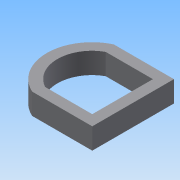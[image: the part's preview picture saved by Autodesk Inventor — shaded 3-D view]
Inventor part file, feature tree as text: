
AUTODESK INVENTOR PART (.ipt)
format: ipt  version: 2015 (Build 190159000, 159)  size: 97,280 bytes
history: native  units: in
note: dims shown in document units (in); Inventor stores cm internally (conversion verified against a paired STEP export)
features: extrude x1, sketch x1
ambient origin geometry x8: Origin, YZ Plane, XZ Plane, XY Plane, X Axis, Y Axis, Z Axis, Center Point
bodies: Body1 (feature_tree)
feature tree (2):
  extrude  "Extrusion2"  Depth=0.25in
  sketch  "Sketch1"  dims[d0=0.41in d1=0.56in d2=0.72in d3=0.573in d4=0.55in d5=0.71in d6=0.6in d7=0.55in d8=0.71in d10=0.55in d11=0.71in d13=0.125in d14=0.125in d15=0.125in d19=0.41in d20=0.125in d21=0.25in d22=0.0in]
